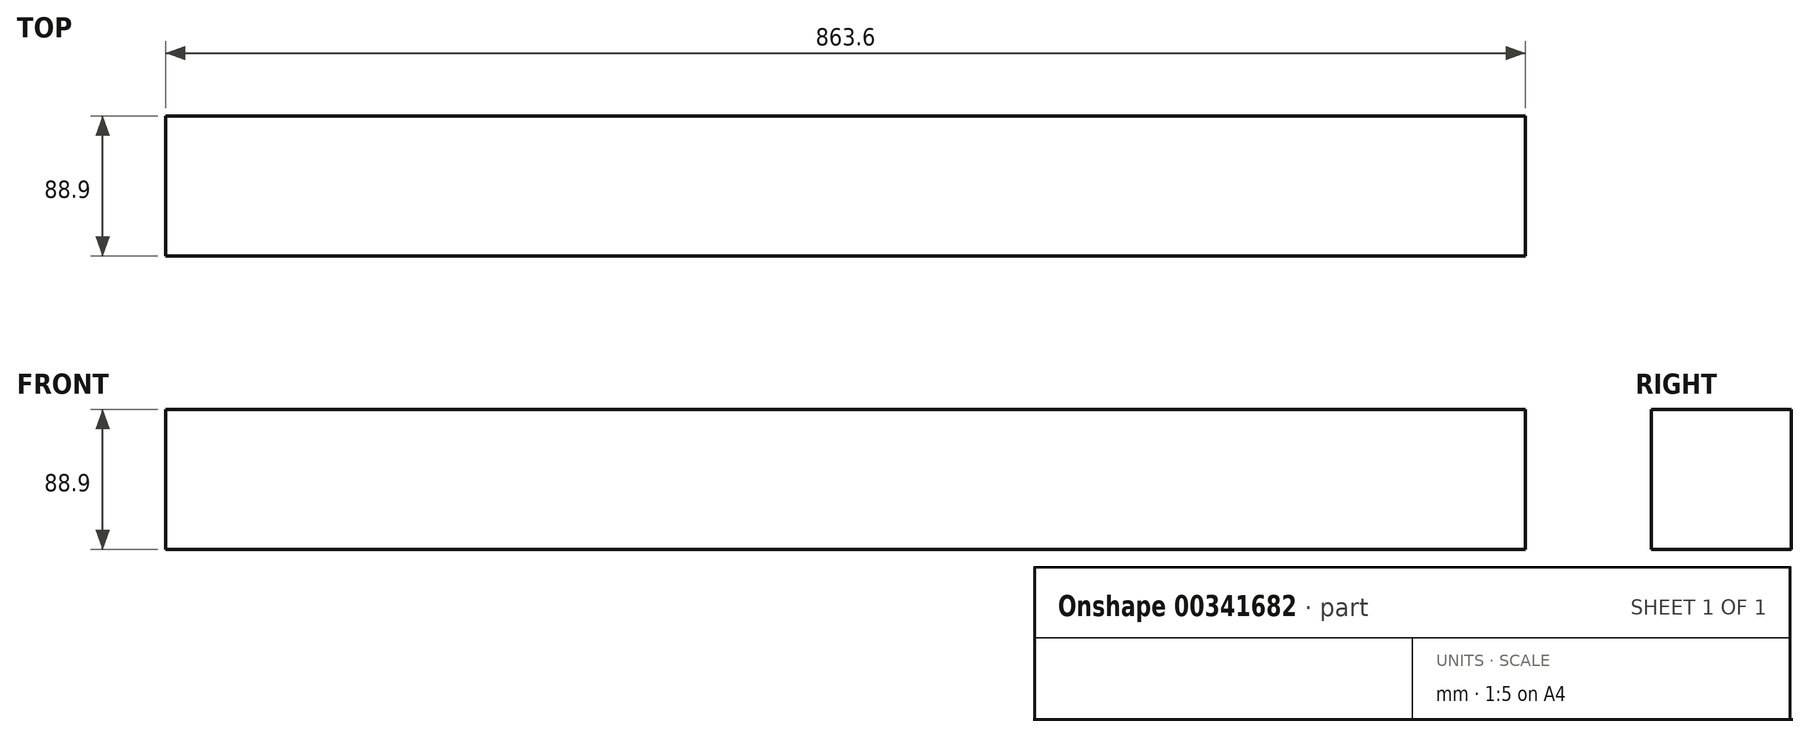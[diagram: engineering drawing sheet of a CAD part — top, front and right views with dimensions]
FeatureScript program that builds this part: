
annotation { "Feature Type Name" : "Feature", "Feature Type Description" : "" }
export const myFeature = defineFeature(function(context is Context, id is Id, definition is map)
    precondition{}
    {
        {
            var Q0;
            Q0=qCreatedBy(makeId("Front.planeOp"),FACE);
            var sketch = newSketch(context, id + "F0", { "sketchPlane" : qUnion([Q0])});
            skLineSegment(sketch, "E0.bottom", {"start": v(-426.76, 30.84) * mm, "end": v(436.84, 30.84) * mm});
            skLineSegment(sketch, "E0.top", {"start": v(-426.76, -58.06) * mm, "end": v(436.84, -58.06) * mm});
            skLineSegment(sketch, "E0.left", {"start": v(-426.76, 30.84) * mm, "end": v(-426.76, -58.06) * mm});
            skLineSegment(sketch, "E0.right", {"start": v(436.84, 30.84) * mm, "end": v(436.84, -58.06) * mm});
            skSolve(sketch);
        }
        {
            var Q0;
            Q0=makeQuery(id+"F0.imprint","IMPRINT",FACE,{"disambiguationData":[TD([[makeQuery(id+"F0.imprint","IMPRINT",EDGE,{"derivedFrom":sQuery(id+"F0.wireOp",EDGE,"E0.bottom")}),-1.0]])]});
            extrude(context, id + "F1", {"entities" : qUnion([Q0]), "depth" : 88.9 * mm});
        }
    });
